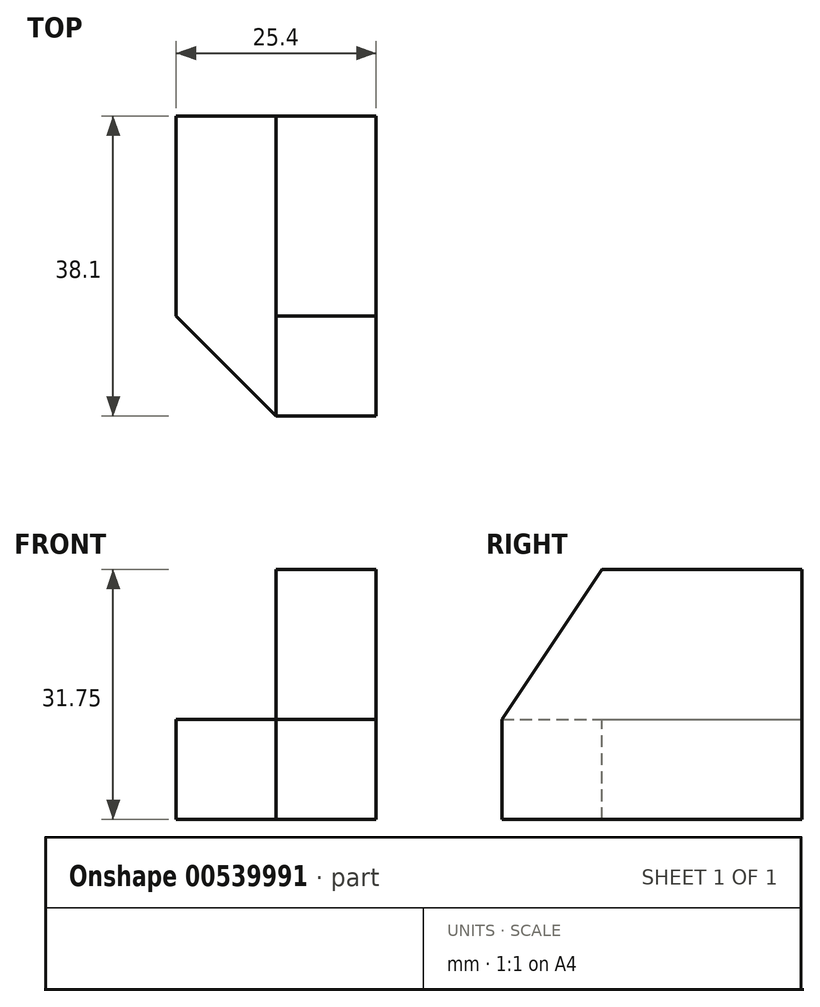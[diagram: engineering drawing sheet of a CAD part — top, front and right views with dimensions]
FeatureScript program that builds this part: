
annotation { "Feature Type Name" : "Feature", "Feature Type Description" : "" }
export const myFeature = defineFeature(function(context is Context, id is Id, definition is map)
    precondition{}
    {
        {
            var Q0;
            Q0=qCreatedBy(makeId("Front.planeOp"),FACE);
            var sketch = newSketch(context, id + "F0", { "sketchPlane" : qUnion([Q0])});
            skLineSegment(sketch, "E0", {"start": v(7.12, 48.18) * mm, "end": v(19.82, 48.18) * mm});
            skLineSegment(sketch, "E1", {"start": v(19.82, 48.18) * mm, "end": v(19.82, 16.43) * mm});
            skLineSegment(sketch, "E2", {"start": v(19.82, 16.43) * mm, "end": v(-5.58, 16.43) * mm});
            skLineSegment(sketch, "E3", {"start": v(-5.58, 16.43) * mm, "end": v(-5.58, 29.13) * mm});
            skLineSegment(sketch, "E4", {"start": v(-5.58, 29.13) * mm, "end": v(7.12, 29.13) * mm});
            skLineSegment(sketch, "E5", {"start": v(7.12, 48.18) * mm, "end": v(7.12, 29.13) * mm});
            skSolve(sketch);
        }
        {
            var Q0;
            Q0 = qSketchRegion(id + "F0", true);
            extrude(context, id + "F1", {"entities" : qUnion([Q0]), "depth" : 38.1 * mm, "offsetDistance" : 25.4 * mm});
        }
        {
            var Q0;
            Q0=makeQuery(id+"F1.opExtrude","CAP_FACE",FACE,{"disambiguationData":[OSD([sQuery(id+"F0.wireOp",EDGE,"E0"),sQuery(id+"F0.wireOp",EDGE,"E1"),sQuery(id+"F0.wireOp",EDGE,"E2"),sQuery(id+"F0.wireOp",EDGE,"E3"),sQuery(id+"F0.wireOp",EDGE,"E4"),sQuery(id+"F0.wireOp",EDGE,"E5")])],"isStart":false});
            var sketch = newSketch(context, id + "F2", { "sketchPlane" : qUnion([Q0])});
            skLineSegment(sketch, "E6", {"start": v(7.12, 29.13) * mm, "end": v(19.82, 29.13) * mm});
            skLineSegment(sketch, "E7", {"start": v(7.12, 29.13) * mm, "end": v(7.12, 16.43) * mm});
            skSolve(sketch);
        }
        {
            var Q0;
            Q0=makeQuery(id+"F1.opExtrude","SWEPT_FACE",FACE,{"disambiguationData":[OSD([sQuery(id+"F0.wireOp",EDGE,"E1")])]});
            var sketch = newSketch(context, id + "F3", { "sketchPlane" : qUnion([Q0])});
            skLineSegment(sketch, "E8", {"start": v(-25.4, 48.18) * mm, "end": v(-38.1, 29.13) * mm});
            skSolve(sketch);
        }
        {
            var Q0;
            {var subQ0=sQuery(id+"F3.wireOp",EDGE,"E8");Q0=makeQuery(id+"F3.imprint","IMPRINT",FACE,{"disambiguationData":[TD([[makeQuery(id+"F3.imprint","IMPRINT",EDGE,{"derivedFrom":subQ0}),-1.0]])]});}
            extrude(context, id + "F4", {"entities" : qUnion([Q0]), "operationType" : NewBodyOperationType.REMOVE, "oppositeDirection" : true, "depth" : 12.7 * mm, "offsetDistance" : 25.4 * mm});
        }
        {
            var Q0;
            Q0=makeQuery(id+"F1.opExtrude","SWEPT_FACE",FACE,{"disambiguationData":[OSD([sQuery(id+"F0.wireOp",EDGE,"E4")])]});
            var sketch = newSketch(context, id + "F5", { "sketchPlane" : qUnion([Q0])});
            skLineSegment(sketch, "E9", {"start": v(7.12, -38.1) * mm, "end": v(-5.58, -25.4) * mm});
            skSolve(sketch);
        }
        {
            var Q0;
            {var subQ0=sQuery(id+"F5.wireOp",EDGE,"E9");Q0=makeQuery(id+"F5.imprint","IMPRINT",FACE,{"disambiguationData":[TD([[makeQuery(id+"F5.imprint","IMPRINT",EDGE,{"derivedFrom":subQ0}),1.0]])]});}
            extrude(context, id + "F6", {"entities" : qUnion([Q0]), "operationType" : NewBodyOperationType.REMOVE, "oppositeDirection" : true, "depth" : 12.7 * mm, "offsetDistance" : 25.4 * mm});
        }
    });
